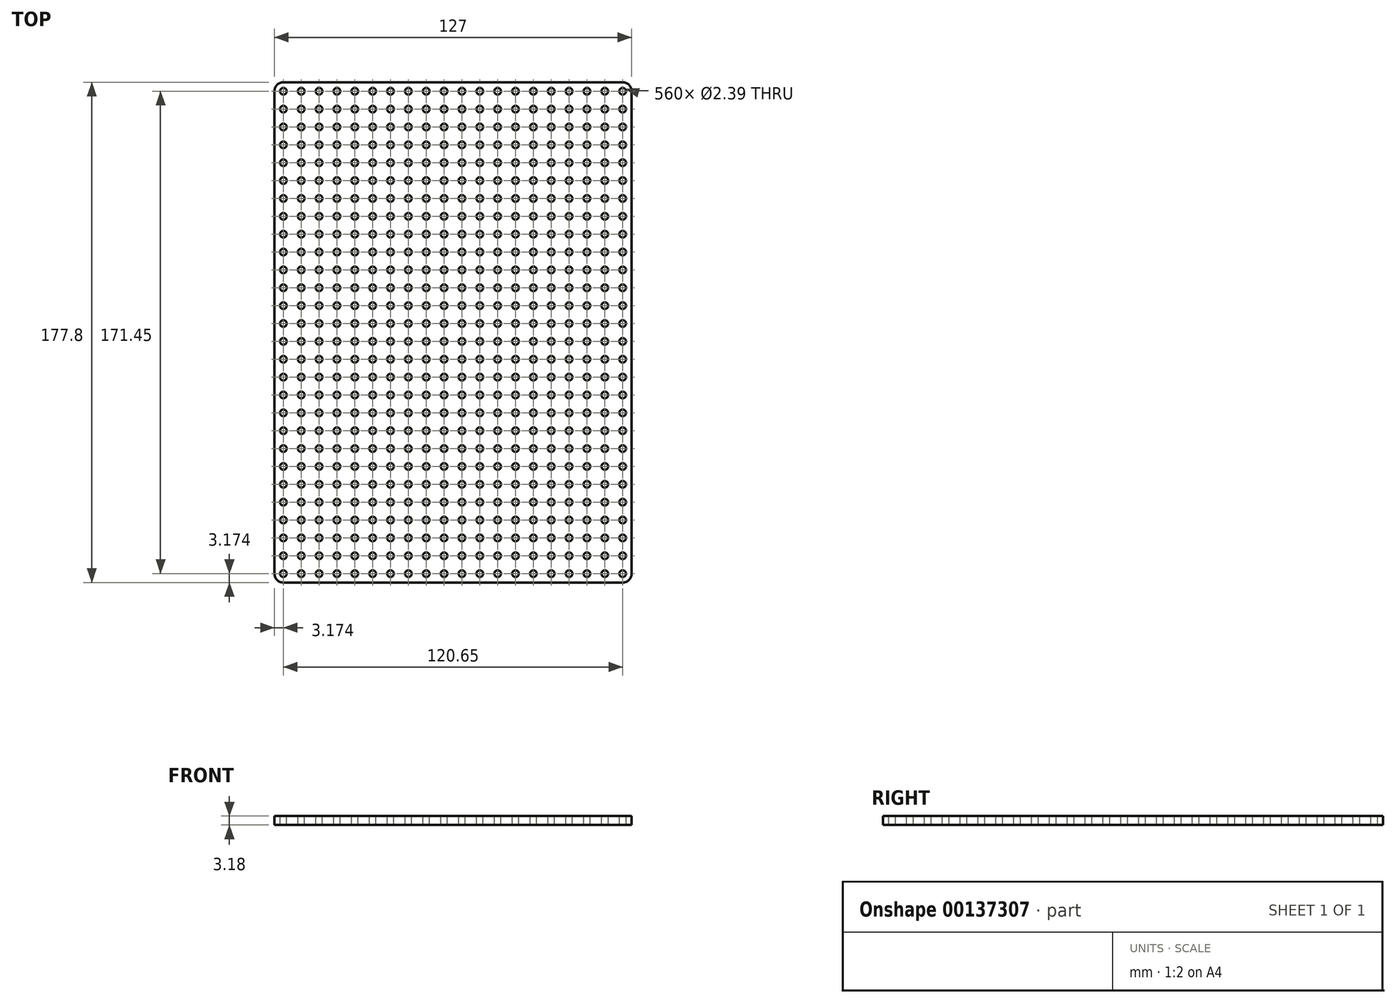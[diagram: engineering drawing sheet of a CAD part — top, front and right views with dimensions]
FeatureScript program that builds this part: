
annotation { "Feature Type Name" : "Feature", "Feature Type Description" : "" }
export const myFeature = defineFeature(function(context is Context, id is Id, definition is map)
    precondition{}
    {
        {
            var Q0;
            Q0=qCreatedBy(makeId("Top.planeOp"),FACE);
            var sketch = newSketch(context, id + "F0", { "sketchPlane" : qUnion([Q0])});
            skLineSegment(sketch, "E0.bottom", {"start": v(-60.72, -89.16) * mm, "end": v(59.93, -89.16) * mm});
            skLineSegment(sketch, "E0.top", {"start": v(-60.72, 88.64) * mm, "end": v(59.93, 88.64) * mm});
            skLineSegment(sketch, "E0.left", {"start": v(-63.9, -85.99) * mm, "end": v(-63.9, 85.46) * mm});
            skLineSegment(sketch, "E0.right", {"start": v(63.1, -85.99) * mm, "end": v(63.1, 85.46) * mm});
            skPoint(sketch, "E1.visualSharp", {"position": v(-63.9, 88.64) * mm});
            skArc(sketch, "E1.filletArc", {"start": v(-60.72, 88.64) * mm, "mid": v(-62.96, 87.7) * mm, "end": v(-63.9, 85.46) * mm});
            skPoint(sketch, "E2.visualSharp", {"position": v(63.1, 88.64) * mm});
            skArc(sketch, "E2.filletArc", {"start": v(63.1, 85.46) * mm, "mid": v(62.18, 87.7) * mm, "end": v(59.93, 88.64) * mm});
            skPoint(sketch, "E3.visualSharp", {"position": v(63.1, -89.16) * mm});
            skArc(sketch, "E3.filletArc", {"start": v(59.93, -89.16) * mm, "mid": v(62.18, -88.23) * mm, "end": v(63.1, -85.99) * mm});
            skPoint(sketch, "E4.visualSharp", {"position": v(-63.9, -89.16) * mm});
            skArc(sketch, "E4.filletArc", {"start": v(-63.9, -85.99) * mm, "mid": v(-62.96, -88.23) * mm, "end": v(-60.72, -89.16) * mm});
            skSolve(sketch);
        }
        {
            var Q0;
            Q0 = qSketchRegion(id + "F0", true);
            extrude(context, id + "F1", {"entities" : qUnion([Q0]), "depth" : 3.17 * mm});
        }
        {
            var Q0;
            Q0=makeQuery(id+"F1.opExtrude","CAP_FACE",FACE,{"disambiguationData":[OSD([sQuery(id+"F0.wireOp",EDGE,"E0.bottom"),sQuery(id+"F0.wireOp",EDGE,"E0.top"),sQuery(id+"F0.wireOp",EDGE,"E0.left"),sQuery(id+"F0.wireOp",EDGE,"E0.right"),sQuery(id+"F0.wireOp",EDGE,"E1.filletArc"),sQuery(id+"F0.wireOp",EDGE,"E2.filletArc"),sQuery(id+"F0.wireOp",EDGE,"E3.filletArc"),sQuery(id+"F0.wireOp",EDGE,"E4.filletArc")])],"isStart":false});
            var sketch = newSketch(context, id + "F2", { "sketchPlane" : qUnion([Q0])});
            skCircle(sketch, "E5", {"center": v(-60.72, -85.99) * mm, "radius": 1.2 * mm});
            skCircle(sketch, "E6.0.1.0", {"center": v(-60.72, -79.64) * mm, "radius": 1.2 * mm});
            skCircle(sketch, "E6.0.2.0", {"center": v(-60.72, -73.29) * mm, "radius": 1.2 * mm});
            skCircle(sketch, "E6.0.3.0", {"center": v(-60.72, -66.94) * mm, "radius": 1.2 * mm});
            skCircle(sketch, "E6.0.4.0", {"center": v(-60.72, -60.59) * mm, "radius": 1.2 * mm});
            skCircle(sketch, "E6.0.5.0", {"center": v(-60.72, -54.24) * mm, "radius": 1.2 * mm});
            skCircle(sketch, "E6.0.6.0", {"center": v(-60.72, -47.89) * mm, "radius": 1.2 * mm});
            skCircle(sketch, "E6.0.7.0", {"center": v(-60.72, -41.54) * mm, "radius": 1.2 * mm});
            skCircle(sketch, "E6.0.8.0", {"center": v(-60.72, -35.19) * mm, "radius": 1.2 * mm});
            skCircle(sketch, "E6.0.9.0", {"center": v(-60.72, -28.84) * mm, "radius": 1.2 * mm});
            skCircle(sketch, "E6.0.10.0", {"center": v(-60.72, -22.49) * mm, "radius": 1.2 * mm});
            skCircle(sketch, "E6.0.11.0", {"center": v(-60.72, -16.14) * mm, "radius": 1.2 * mm});
            skCircle(sketch, "E6.0.12.0", {"center": v(-60.72, -9.79) * mm, "radius": 1.2 * mm});
            skCircle(sketch, "E6.0.13.0", {"center": v(-60.72, -3.44) * mm, "radius": 1.2 * mm});
            skCircle(sketch, "E6.0.14.0", {"center": v(-60.72, 2.91) * mm, "radius": 1.2 * mm});
            skCircle(sketch, "E6.0.15.0", {"center": v(-60.72, 9.26) * mm, "radius": 1.2 * mm});
            skCircle(sketch, "E6.0.16.0", {"center": v(-60.72, 15.61) * mm, "radius": 1.2 * mm});
            skCircle(sketch, "E6.0.17.0", {"center": v(-60.72, 21.96) * mm, "radius": 1.2 * mm});
            skCircle(sketch, "E6.0.18.0", {"center": v(-60.72, 28.31) * mm, "radius": 1.2 * mm});
            skCircle(sketch, "E6.0.19.0", {"center": v(-60.72, 34.66) * mm, "radius": 1.2 * mm});
            skCircle(sketch, "E6.0.20.0", {"center": v(-60.72, 41.01) * mm, "radius": 1.2 * mm});
            skCircle(sketch, "E6.0.21.0", {"center": v(-60.72, 47.36) * mm, "radius": 1.2 * mm});
            skCircle(sketch, "E6.0.22.0", {"center": v(-60.72, 53.71) * mm, "radius": 1.2 * mm});
            skCircle(sketch, "E6.0.23.0", {"center": v(-60.72, 60.06) * mm, "radius": 1.2 * mm});
            skCircle(sketch, "E6.0.24.0", {"center": v(-60.72, 66.41) * mm, "radius": 1.2 * mm});
            skCircle(sketch, "E6.0.25.0", {"center": v(-60.72, 72.76) * mm, "radius": 1.2 * mm});
            skCircle(sketch, "E6.0.26.0", {"center": v(-60.72, 79.11) * mm, "radius": 1.2 * mm});
            skCircle(sketch, "E6.0.27.0", {"center": v(-60.72, 85.46) * mm, "radius": 1.2 * mm});
            skCircle(sketch, "E6.1.0.0", {"center": v(-54.37, -85.99) * mm, "radius": 1.2 * mm});
            skCircle(sketch, "E6.1.1.0", {"center": v(-54.37, -79.64) * mm, "radius": 1.2 * mm});
            skCircle(sketch, "E6.1.2.0", {"center": v(-54.37, -73.29) * mm, "radius": 1.2 * mm});
            skCircle(sketch, "E6.1.3.0", {"center": v(-54.37, -66.94) * mm, "radius": 1.2 * mm});
            skCircle(sketch, "E6.1.4.0", {"center": v(-54.37, -60.59) * mm, "radius": 1.2 * mm});
            skCircle(sketch, "E6.1.5.0", {"center": v(-54.37, -54.24) * mm, "radius": 1.2 * mm});
            skCircle(sketch, "E6.1.6.0", {"center": v(-54.37, -47.89) * mm, "radius": 1.2 * mm});
            skCircle(sketch, "E6.1.7.0", {"center": v(-54.37, -41.54) * mm, "radius": 1.2 * mm});
            skCircle(sketch, "E6.1.8.0", {"center": v(-54.37, -35.19) * mm, "radius": 1.2 * mm});
            skCircle(sketch, "E6.1.9.0", {"center": v(-54.37, -28.84) * mm, "radius": 1.2 * mm});
            skCircle(sketch, "E6.1.10.0", {"center": v(-54.37, -22.49) * mm, "radius": 1.2 * mm});
            skCircle(sketch, "E6.1.11.0", {"center": v(-54.37, -16.14) * mm, "radius": 1.2 * mm});
            skCircle(sketch, "E6.1.12.0", {"center": v(-54.37, -9.79) * mm, "radius": 1.2 * mm});
            skCircle(sketch, "E6.1.13.0", {"center": v(-54.37, -3.44) * mm, "radius": 1.2 * mm});
            skCircle(sketch, "E6.1.14.0", {"center": v(-54.37, 2.91) * mm, "radius": 1.2 * mm});
            skCircle(sketch, "E6.1.15.0", {"center": v(-54.37, 9.26) * mm, "radius": 1.2 * mm});
            skCircle(sketch, "E6.1.16.0", {"center": v(-54.37, 15.61) * mm, "radius": 1.2 * mm});
            skCircle(sketch, "E6.1.17.0", {"center": v(-54.37, 21.96) * mm, "radius": 1.2 * mm});
            skCircle(sketch, "E6.1.18.0", {"center": v(-54.37, 28.31) * mm, "radius": 1.2 * mm});
            skCircle(sketch, "E6.1.19.0", {"center": v(-54.37, 34.66) * mm, "radius": 1.2 * mm});
            skCircle(sketch, "E6.1.20.0", {"center": v(-54.37, 41.01) * mm, "radius": 1.2 * mm});
            skCircle(sketch, "E6.1.21.0", {"center": v(-54.37, 47.36) * mm, "radius": 1.2 * mm});
            skCircle(sketch, "E6.1.22.0", {"center": v(-54.37, 53.71) * mm, "radius": 1.2 * mm});
            skCircle(sketch, "E6.1.23.0", {"center": v(-54.37, 60.06) * mm, "radius": 1.2 * mm});
            skCircle(sketch, "E6.1.24.0", {"center": v(-54.37, 66.41) * mm, "radius": 1.2 * mm});
            skCircle(sketch, "E6.1.25.0", {"center": v(-54.37, 72.76) * mm, "radius": 1.2 * mm});
            skCircle(sketch, "E6.1.26.0", {"center": v(-54.37, 79.11) * mm, "radius": 1.2 * mm});
            skCircle(sketch, "E6.1.27.0", {"center": v(-54.37, 85.46) * mm, "radius": 1.2 * mm});
            skCircle(sketch, "E6.2.0.0", {"center": v(-48.02, -85.99) * mm, "radius": 1.2 * mm});
            skCircle(sketch, "E6.2.1.0", {"center": v(-48.02, -79.64) * mm, "radius": 1.2 * mm});
            skCircle(sketch, "E6.2.2.0", {"center": v(-48.02, -73.29) * mm, "radius": 1.2 * mm});
            skCircle(sketch, "E6.2.3.0", {"center": v(-48.02, -66.94) * mm, "radius": 1.2 * mm});
            skCircle(sketch, "E6.2.4.0", {"center": v(-48.02, -60.59) * mm, "radius": 1.2 * mm});
            skCircle(sketch, "E6.2.5.0", {"center": v(-48.02, -54.24) * mm, "radius": 1.2 * mm});
            skCircle(sketch, "E6.2.6.0", {"center": v(-48.02, -47.89) * mm, "radius": 1.2 * mm});
            skCircle(sketch, "E6.2.7.0", {"center": v(-48.02, -41.54) * mm, "radius": 1.2 * mm});
            skCircle(sketch, "E6.2.8.0", {"center": v(-48.02, -35.19) * mm, "radius": 1.2 * mm});
            skCircle(sketch, "E6.2.9.0", {"center": v(-48.02, -28.84) * mm, "radius": 1.2 * mm});
            skCircle(sketch, "E6.2.10.0", {"center": v(-48.02, -22.49) * mm, "radius": 1.2 * mm});
            skCircle(sketch, "E6.2.11.0", {"center": v(-48.02, -16.14) * mm, "radius": 1.2 * mm});
            skCircle(sketch, "E6.2.12.0", {"center": v(-48.02, -9.79) * mm, "radius": 1.2 * mm});
            skCircle(sketch, "E6.2.13.0", {"center": v(-48.02, -3.44) * mm, "radius": 1.2 * mm});
            skCircle(sketch, "E6.2.14.0", {"center": v(-48.02, 2.91) * mm, "radius": 1.2 * mm});
            skCircle(sketch, "E6.2.15.0", {"center": v(-48.02, 9.26) * mm, "radius": 1.2 * mm});
            skCircle(sketch, "E6.2.16.0", {"center": v(-48.02, 15.61) * mm, "radius": 1.2 * mm});
            skCircle(sketch, "E6.2.17.0", {"center": v(-48.02, 21.96) * mm, "radius": 1.2 * mm});
            skCircle(sketch, "E6.2.18.0", {"center": v(-48.02, 28.31) * mm, "radius": 1.2 * mm});
            skCircle(sketch, "E6.2.19.0", {"center": v(-48.02, 34.66) * mm, "radius": 1.2 * mm});
            skCircle(sketch, "E6.2.20.0", {"center": v(-48.02, 41.01) * mm, "radius": 1.2 * mm});
            skCircle(sketch, "E6.2.21.0", {"center": v(-48.02, 47.36) * mm, "radius": 1.2 * mm});
            skCircle(sketch, "E6.2.22.0", {"center": v(-48.02, 53.71) * mm, "radius": 1.2 * mm});
            skCircle(sketch, "E6.2.23.0", {"center": v(-48.02, 60.06) * mm, "radius": 1.2 * mm});
            skCircle(sketch, "E6.2.24.0", {"center": v(-48.02, 66.41) * mm, "radius": 1.2 * mm});
            skCircle(sketch, "E6.2.25.0", {"center": v(-48.02, 72.76) * mm, "radius": 1.2 * mm});
            skCircle(sketch, "E6.2.26.0", {"center": v(-48.02, 79.11) * mm, "radius": 1.2 * mm});
            skCircle(sketch, "E6.2.27.0", {"center": v(-48.02, 85.46) * mm, "radius": 1.2 * mm});
            skCircle(sketch, "E6.3.0.0", {"center": v(-41.67, -85.99) * mm, "radius": 1.2 * mm});
            skCircle(sketch, "E6.3.1.0", {"center": v(-41.67, -79.64) * mm, "radius": 1.2 * mm});
            skCircle(sketch, "E6.3.2.0", {"center": v(-41.67, -73.29) * mm, "radius": 1.2 * mm});
            skCircle(sketch, "E6.3.3.0", {"center": v(-41.67, -66.94) * mm, "radius": 1.2 * mm});
            skCircle(sketch, "E6.3.4.0", {"center": v(-41.67, -60.59) * mm, "radius": 1.2 * mm});
            skCircle(sketch, "E6.3.5.0", {"center": v(-41.67, -54.24) * mm, "radius": 1.2 * mm});
            skCircle(sketch, "E6.3.6.0", {"center": v(-41.67, -47.89) * mm, "radius": 1.2 * mm});
            skCircle(sketch, "E6.3.7.0", {"center": v(-41.67, -41.54) * mm, "radius": 1.2 * mm});
            skCircle(sketch, "E6.3.8.0", {"center": v(-41.67, -35.19) * mm, "radius": 1.2 * mm});
            skCircle(sketch, "E6.3.9.0", {"center": v(-41.67, -28.84) * mm, "radius": 1.2 * mm});
            skCircle(sketch, "E6.3.10.0", {"center": v(-41.67, -22.49) * mm, "radius": 1.2 * mm});
            skCircle(sketch, "E6.3.11.0", {"center": v(-41.67, -16.14) * mm, "radius": 1.2 * mm});
            skCircle(sketch, "E6.3.12.0", {"center": v(-41.67, -9.79) * mm, "radius": 1.2 * mm});
            skCircle(sketch, "E6.3.13.0", {"center": v(-41.67, -3.44) * mm, "radius": 1.2 * mm});
            skCircle(sketch, "E6.3.14.0", {"center": v(-41.67, 2.91) * mm, "radius": 1.2 * mm});
            skCircle(sketch, "E6.3.15.0", {"center": v(-41.67, 9.26) * mm, "radius": 1.2 * mm});
            skCircle(sketch, "E6.3.16.0", {"center": v(-41.67, 15.61) * mm, "radius": 1.2 * mm});
            skCircle(sketch, "E6.3.17.0", {"center": v(-41.67, 21.96) * mm, "radius": 1.2 * mm});
            skCircle(sketch, "E6.3.18.0", {"center": v(-41.67, 28.31) * mm, "radius": 1.2 * mm});
            skCircle(sketch, "E6.3.19.0", {"center": v(-41.67, 34.66) * mm, "radius": 1.2 * mm});
            skCircle(sketch, "E6.3.20.0", {"center": v(-41.67, 41.01) * mm, "radius": 1.2 * mm});
            skCircle(sketch, "E6.3.21.0", {"center": v(-41.67, 47.36) * mm, "radius": 1.2 * mm});
            skCircle(sketch, "E6.3.22.0", {"center": v(-41.67, 53.71) * mm, "radius": 1.2 * mm});
            skCircle(sketch, "E6.3.23.0", {"center": v(-41.67, 60.06) * mm, "radius": 1.2 * mm});
            skCircle(sketch, "E6.3.24.0", {"center": v(-41.67, 66.41) * mm, "radius": 1.2 * mm});
            skCircle(sketch, "E6.3.25.0", {"center": v(-41.67, 72.76) * mm, "radius": 1.2 * mm});
            skCircle(sketch, "E6.3.26.0", {"center": v(-41.67, 79.11) * mm, "radius": 1.2 * mm});
            skCircle(sketch, "E6.3.27.0", {"center": v(-41.67, 85.46) * mm, "radius": 1.2 * mm});
            skCircle(sketch, "E6.4.0.0", {"center": v(-35.32, -85.99) * mm, "radius": 1.2 * mm});
            skCircle(sketch, "E6.4.1.0", {"center": v(-35.32, -79.64) * mm, "radius": 1.2 * mm});
            skCircle(sketch, "E6.4.2.0", {"center": v(-35.32, -73.29) * mm, "radius": 1.2 * mm});
            skCircle(sketch, "E6.4.3.0", {"center": v(-35.32, -66.94) * mm, "radius": 1.2 * mm});
            skCircle(sketch, "E6.4.4.0", {"center": v(-35.32, -60.59) * mm, "radius": 1.2 * mm});
            skCircle(sketch, "E6.4.5.0", {"center": v(-35.32, -54.24) * mm, "radius": 1.2 * mm});
            skCircle(sketch, "E6.4.6.0", {"center": v(-35.32, -47.89) * mm, "radius": 1.2 * mm});
            skCircle(sketch, "E6.4.7.0", {"center": v(-35.32, -41.54) * mm, "radius": 1.2 * mm});
            skCircle(sketch, "E6.4.8.0", {"center": v(-35.32, -35.19) * mm, "radius": 1.2 * mm});
            skCircle(sketch, "E6.4.9.0", {"center": v(-35.32, -28.84) * mm, "radius": 1.2 * mm});
            skCircle(sketch, "E6.4.10.0", {"center": v(-35.32, -22.49) * mm, "radius": 1.2 * mm});
            skCircle(sketch, "E6.4.11.0", {"center": v(-35.32, -16.14) * mm, "radius": 1.2 * mm});
            skCircle(sketch, "E6.4.12.0", {"center": v(-35.32, -9.79) * mm, "radius": 1.2 * mm});
            skCircle(sketch, "E6.4.13.0", {"center": v(-35.32, -3.44) * mm, "radius": 1.2 * mm});
            skCircle(sketch, "E6.4.14.0", {"center": v(-35.32, 2.91) * mm, "radius": 1.2 * mm});
            skCircle(sketch, "E6.4.15.0", {"center": v(-35.32, 9.26) * mm, "radius": 1.2 * mm});
            skCircle(sketch, "E6.4.16.0", {"center": v(-35.32, 15.61) * mm, "radius": 1.2 * mm});
            skCircle(sketch, "E6.4.17.0", {"center": v(-35.32, 21.96) * mm, "radius": 1.2 * mm});
            skCircle(sketch, "E6.4.18.0", {"center": v(-35.32, 28.31) * mm, "radius": 1.2 * mm});
            skCircle(sketch, "E6.4.19.0", {"center": v(-35.32, 34.66) * mm, "radius": 1.2 * mm});
            skCircle(sketch, "E6.4.20.0", {"center": v(-35.32, 41.01) * mm, "radius": 1.2 * mm});
            skCircle(sketch, "E6.4.21.0", {"center": v(-35.32, 47.36) * mm, "radius": 1.2 * mm});
            skCircle(sketch, "E6.4.22.0", {"center": v(-35.32, 53.71) * mm, "radius": 1.2 * mm});
            skCircle(sketch, "E6.4.23.0", {"center": v(-35.32, 60.06) * mm, "radius": 1.2 * mm});
            skCircle(sketch, "E6.4.24.0", {"center": v(-35.32, 66.41) * mm, "radius": 1.2 * mm});
            skCircle(sketch, "E6.4.25.0", {"center": v(-35.32, 72.76) * mm, "radius": 1.2 * mm});
            skCircle(sketch, "E6.4.26.0", {"center": v(-35.32, 79.11) * mm, "radius": 1.2 * mm});
            skCircle(sketch, "E6.4.27.0", {"center": v(-35.32, 85.46) * mm, "radius": 1.2 * mm});
            skCircle(sketch, "E6.5.0.0", {"center": v(-28.97, -85.99) * mm, "radius": 1.2 * mm});
            skCircle(sketch, "E6.5.1.0", {"center": v(-28.97, -79.64) * mm, "radius": 1.2 * mm});
            skCircle(sketch, "E6.5.2.0", {"center": v(-28.97, -73.29) * mm, "radius": 1.2 * mm});
            skCircle(sketch, "E6.5.3.0", {"center": v(-28.97, -66.94) * mm, "radius": 1.2 * mm});
            skCircle(sketch, "E6.5.4.0", {"center": v(-28.97, -60.59) * mm, "radius": 1.2 * mm});
            skCircle(sketch, "E6.5.5.0", {"center": v(-28.97, -54.24) * mm, "radius": 1.2 * mm});
            skCircle(sketch, "E6.5.6.0", {"center": v(-28.97, -47.89) * mm, "radius": 1.2 * mm});
            skCircle(sketch, "E6.5.7.0", {"center": v(-28.97, -41.54) * mm, "radius": 1.2 * mm});
            skCircle(sketch, "E6.5.8.0", {"center": v(-28.97, -35.19) * mm, "radius": 1.2 * mm});
            skCircle(sketch, "E6.5.9.0", {"center": v(-28.97, -28.84) * mm, "radius": 1.2 * mm});
            skCircle(sketch, "E6.5.10.0", {"center": v(-28.97, -22.49) * mm, "radius": 1.2 * mm});
            skCircle(sketch, "E6.5.11.0", {"center": v(-28.97, -16.14) * mm, "radius": 1.2 * mm});
            skCircle(sketch, "E6.5.12.0", {"center": v(-28.97, -9.79) * mm, "radius": 1.2 * mm});
            skCircle(sketch, "E6.5.13.0", {"center": v(-28.97, -3.44) * mm, "radius": 1.2 * mm});
            skCircle(sketch, "E6.5.14.0", {"center": v(-28.97, 2.91) * mm, "radius": 1.2 * mm});
            skCircle(sketch, "E6.5.15.0", {"center": v(-28.97, 9.26) * mm, "radius": 1.2 * mm});
            skCircle(sketch, "E6.5.16.0", {"center": v(-28.97, 15.61) * mm, "radius": 1.2 * mm});
            skCircle(sketch, "E6.5.17.0", {"center": v(-28.97, 21.96) * mm, "radius": 1.2 * mm});
            skCircle(sketch, "E6.5.18.0", {"center": v(-28.97, 28.31) * mm, "radius": 1.2 * mm});
            skCircle(sketch, "E6.5.19.0", {"center": v(-28.97, 34.66) * mm, "radius": 1.2 * mm});
            skCircle(sketch, "E6.5.20.0", {"center": v(-28.97, 41.01) * mm, "radius": 1.2 * mm});
            skCircle(sketch, "E6.5.21.0", {"center": v(-28.97, 47.36) * mm, "radius": 1.2 * mm});
            skCircle(sketch, "E6.5.22.0", {"center": v(-28.97, 53.71) * mm, "radius": 1.2 * mm});
            skCircle(sketch, "E6.5.23.0", {"center": v(-28.97, 60.06) * mm, "radius": 1.2 * mm});
            skCircle(sketch, "E6.5.24.0", {"center": v(-28.97, 66.41) * mm, "radius": 1.2 * mm});
            skCircle(sketch, "E6.5.25.0", {"center": v(-28.97, 72.76) * mm, "radius": 1.2 * mm});
            skCircle(sketch, "E6.5.26.0", {"center": v(-28.97, 79.11) * mm, "radius": 1.2 * mm});
            skCircle(sketch, "E6.5.27.0", {"center": v(-28.97, 85.46) * mm, "radius": 1.2 * mm});
            skCircle(sketch, "E6.6.0.0", {"center": v(-22.62, -85.99) * mm, "radius": 1.2 * mm});
            skCircle(sketch, "E6.6.1.0", {"center": v(-22.62, -79.64) * mm, "radius": 1.2 * mm});
            skCircle(sketch, "E6.6.2.0", {"center": v(-22.62, -73.29) * mm, "radius": 1.2 * mm});
            skCircle(sketch, "E6.6.3.0", {"center": v(-22.62, -66.94) * mm, "radius": 1.2 * mm});
            skCircle(sketch, "E6.6.4.0", {"center": v(-22.62, -60.59) * mm, "radius": 1.2 * mm});
            skCircle(sketch, "E6.6.5.0", {"center": v(-22.62, -54.24) * mm, "radius": 1.2 * mm});
            skCircle(sketch, "E6.6.6.0", {"center": v(-22.62, -47.89) * mm, "radius": 1.2 * mm});
            skCircle(sketch, "E6.6.7.0", {"center": v(-22.62, -41.54) * mm, "radius": 1.2 * mm});
            skCircle(sketch, "E6.6.8.0", {"center": v(-22.62, -35.19) * mm, "radius": 1.2 * mm});
            skCircle(sketch, "E6.6.9.0", {"center": v(-22.62, -28.84) * mm, "radius": 1.2 * mm});
            skCircle(sketch, "E6.6.10.0", {"center": v(-22.62, -22.49) * mm, "radius": 1.2 * mm});
            skCircle(sketch, "E6.6.11.0", {"center": v(-22.62, -16.14) * mm, "radius": 1.2 * mm});
            skCircle(sketch, "E6.6.12.0", {"center": v(-22.62, -9.79) * mm, "radius": 1.2 * mm});
            skCircle(sketch, "E6.6.13.0", {"center": v(-22.62, -3.44) * mm, "radius": 1.2 * mm});
            skCircle(sketch, "E6.6.14.0", {"center": v(-22.62, 2.91) * mm, "radius": 1.2 * mm});
            skCircle(sketch, "E6.6.15.0", {"center": v(-22.62, 9.26) * mm, "radius": 1.2 * mm});
            skCircle(sketch, "E6.6.16.0", {"center": v(-22.62, 15.61) * mm, "radius": 1.2 * mm});
            skCircle(sketch, "E6.6.17.0", {"center": v(-22.62, 21.96) * mm, "radius": 1.2 * mm});
            skCircle(sketch, "E6.6.18.0", {"center": v(-22.62, 28.31) * mm, "radius": 1.2 * mm});
            skCircle(sketch, "E6.6.19.0", {"center": v(-22.62, 34.66) * mm, "radius": 1.2 * mm});
            skCircle(sketch, "E6.6.20.0", {"center": v(-22.62, 41.01) * mm, "radius": 1.2 * mm});
            skCircle(sketch, "E6.6.21.0", {"center": v(-22.62, 47.36) * mm, "radius": 1.2 * mm});
            skCircle(sketch, "E6.6.22.0", {"center": v(-22.62, 53.71) * mm, "radius": 1.2 * mm});
            skCircle(sketch, "E6.6.23.0", {"center": v(-22.62, 60.06) * mm, "radius": 1.2 * mm});
            skCircle(sketch, "E6.6.24.0", {"center": v(-22.62, 66.41) * mm, "radius": 1.2 * mm});
            skCircle(sketch, "E6.6.25.0", {"center": v(-22.62, 72.76) * mm, "radius": 1.2 * mm});
            skCircle(sketch, "E6.6.26.0", {"center": v(-22.62, 79.11) * mm, "radius": 1.2 * mm});
            skCircle(sketch, "E6.6.27.0", {"center": v(-22.62, 85.46) * mm, "radius": 1.2 * mm});
            skCircle(sketch, "E6.7.0.0", {"center": v(-16.27, -85.99) * mm, "radius": 1.2 * mm});
            skCircle(sketch, "E6.7.1.0", {"center": v(-16.27, -79.64) * mm, "radius": 1.2 * mm});
            skCircle(sketch, "E6.7.2.0", {"center": v(-16.27, -73.29) * mm, "radius": 1.2 * mm});
            skCircle(sketch, "E6.7.3.0", {"center": v(-16.27, -66.94) * mm, "radius": 1.2 * mm});
            skCircle(sketch, "E6.7.4.0", {"center": v(-16.27, -60.59) * mm, "radius": 1.2 * mm});
            skCircle(sketch, "E6.7.5.0", {"center": v(-16.27, -54.24) * mm, "radius": 1.2 * mm});
            skCircle(sketch, "E6.7.6.0", {"center": v(-16.27, -47.89) * mm, "radius": 1.2 * mm});
            skCircle(sketch, "E6.7.7.0", {"center": v(-16.27, -41.54) * mm, "radius": 1.2 * mm});
            skCircle(sketch, "E6.7.8.0", {"center": v(-16.27, -35.19) * mm, "radius": 1.2 * mm});
            skCircle(sketch, "E6.7.9.0", {"center": v(-16.27, -28.84) * mm, "radius": 1.2 * mm});
            skCircle(sketch, "E6.7.10.0", {"center": v(-16.27, -22.49) * mm, "radius": 1.2 * mm});
            skCircle(sketch, "E6.7.11.0", {"center": v(-16.27, -16.14) * mm, "radius": 1.2 * mm});
            skCircle(sketch, "E6.7.12.0", {"center": v(-16.27, -9.79) * mm, "radius": 1.2 * mm});
            skCircle(sketch, "E6.7.13.0", {"center": v(-16.27, -3.44) * mm, "radius": 1.2 * mm});
            skCircle(sketch, "E6.7.14.0", {"center": v(-16.27, 2.91) * mm, "radius": 1.2 * mm});
            skCircle(sketch, "E6.7.15.0", {"center": v(-16.27, 9.26) * mm, "radius": 1.2 * mm});
            skCircle(sketch, "E6.7.16.0", {"center": v(-16.27, 15.61) * mm, "radius": 1.2 * mm});
            skCircle(sketch, "E6.7.17.0", {"center": v(-16.27, 21.96) * mm, "radius": 1.2 * mm});
            skCircle(sketch, "E6.7.18.0", {"center": v(-16.27, 28.31) * mm, "radius": 1.2 * mm});
            skCircle(sketch, "E6.7.19.0", {"center": v(-16.27, 34.66) * mm, "radius": 1.2 * mm});
            skCircle(sketch, "E6.7.20.0", {"center": v(-16.27, 41.01) * mm, "radius": 1.2 * mm});
            skCircle(sketch, "E6.7.21.0", {"center": v(-16.27, 47.36) * mm, "radius": 1.2 * mm});
            skCircle(sketch, "E6.7.22.0", {"center": v(-16.27, 53.71) * mm, "radius": 1.2 * mm});
            skCircle(sketch, "E6.7.23.0", {"center": v(-16.27, 60.06) * mm, "radius": 1.2 * mm});
            skCircle(sketch, "E6.7.24.0", {"center": v(-16.27, 66.41) * mm, "radius": 1.2 * mm});
            skCircle(sketch, "E6.7.25.0", {"center": v(-16.27, 72.76) * mm, "radius": 1.2 * mm});
            skCircle(sketch, "E6.7.26.0", {"center": v(-16.27, 79.11) * mm, "radius": 1.2 * mm});
            skCircle(sketch, "E6.7.27.0", {"center": v(-16.27, 85.46) * mm, "radius": 1.2 * mm});
            skCircle(sketch, "E6.8.0.0", {"center": v(-9.92, -85.99) * mm, "radius": 1.2 * mm});
            skCircle(sketch, "E6.8.1.0", {"center": v(-9.92, -79.64) * mm, "radius": 1.2 * mm});
            skCircle(sketch, "E6.8.2.0", {"center": v(-9.92, -73.29) * mm, "radius": 1.2 * mm});
            skCircle(sketch, "E6.8.3.0", {"center": v(-9.92, -66.94) * mm, "radius": 1.2 * mm});
            skCircle(sketch, "E6.8.4.0", {"center": v(-9.92, -60.59) * mm, "radius": 1.2 * mm});
            skCircle(sketch, "E6.8.5.0", {"center": v(-9.92, -54.24) * mm, "radius": 1.2 * mm});
            skCircle(sketch, "E6.8.6.0", {"center": v(-9.92, -47.89) * mm, "radius": 1.2 * mm});
            skCircle(sketch, "E6.8.7.0", {"center": v(-9.92, -41.54) * mm, "radius": 1.2 * mm});
            skCircle(sketch, "E6.8.8.0", {"center": v(-9.92, -35.19) * mm, "radius": 1.2 * mm});
            skCircle(sketch, "E6.8.9.0", {"center": v(-9.92, -28.84) * mm, "radius": 1.2 * mm});
            skCircle(sketch, "E6.8.10.0", {"center": v(-9.92, -22.49) * mm, "radius": 1.2 * mm});
            skCircle(sketch, "E6.8.11.0", {"center": v(-9.92, -16.14) * mm, "radius": 1.2 * mm});
            skCircle(sketch, "E6.8.12.0", {"center": v(-9.92, -9.79) * mm, "radius": 1.2 * mm});
            skCircle(sketch, "E6.8.13.0", {"center": v(-9.92, -3.44) * mm, "radius": 1.2 * mm});
            skCircle(sketch, "E6.8.14.0", {"center": v(-9.92, 2.91) * mm, "radius": 1.2 * mm});
            skCircle(sketch, "E6.8.15.0", {"center": v(-9.92, 9.26) * mm, "radius": 1.2 * mm});
            skCircle(sketch, "E6.8.16.0", {"center": v(-9.92, 15.61) * mm, "radius": 1.2 * mm});
            skCircle(sketch, "E6.8.17.0", {"center": v(-9.92, 21.96) * mm, "radius": 1.2 * mm});
            skCircle(sketch, "E6.8.18.0", {"center": v(-9.92, 28.31) * mm, "radius": 1.2 * mm});
            skCircle(sketch, "E6.8.19.0", {"center": v(-9.92, 34.66) * mm, "radius": 1.2 * mm});
            skCircle(sketch, "E6.8.20.0", {"center": v(-9.92, 41.01) * mm, "radius": 1.2 * mm});
            skCircle(sketch, "E6.8.21.0", {"center": v(-9.92, 47.36) * mm, "radius": 1.2 * mm});
            skCircle(sketch, "E6.8.22.0", {"center": v(-9.92, 53.71) * mm, "radius": 1.2 * mm});
            skCircle(sketch, "E6.8.23.0", {"center": v(-9.92, 60.06) * mm, "radius": 1.2 * mm});
            skCircle(sketch, "E6.8.24.0", {"center": v(-9.92, 66.41) * mm, "radius": 1.2 * mm});
            skCircle(sketch, "E6.8.25.0", {"center": v(-9.92, 72.76) * mm, "radius": 1.2 * mm});
            skCircle(sketch, "E6.8.26.0", {"center": v(-9.92, 79.11) * mm, "radius": 1.2 * mm});
            skCircle(sketch, "E6.8.27.0", {"center": v(-9.92, 85.46) * mm, "radius": 1.2 * mm});
            skCircle(sketch, "E6.9.0.0", {"center": v(-3.57, -85.99) * mm, "radius": 1.2 * mm});
            skCircle(sketch, "E6.9.1.0", {"center": v(-3.57, -79.64) * mm, "radius": 1.2 * mm});
            skCircle(sketch, "E6.9.2.0", {"center": v(-3.57, -73.29) * mm, "radius": 1.2 * mm});
            skCircle(sketch, "E6.9.3.0", {"center": v(-3.57, -66.94) * mm, "radius": 1.2 * mm});
            skCircle(sketch, "E6.9.4.0", {"center": v(-3.57, -60.59) * mm, "radius": 1.2 * mm});
            skCircle(sketch, "E6.9.5.0", {"center": v(-3.57, -54.24) * mm, "radius": 1.2 * mm});
            skCircle(sketch, "E6.9.6.0", {"center": v(-3.57, -47.89) * mm, "radius": 1.2 * mm});
            skCircle(sketch, "E6.9.7.0", {"center": v(-3.57, -41.54) * mm, "radius": 1.2 * mm});
            skCircle(sketch, "E6.9.8.0", {"center": v(-3.57, -35.19) * mm, "radius": 1.2 * mm});
            skCircle(sketch, "E6.9.9.0", {"center": v(-3.57, -28.84) * mm, "radius": 1.2 * mm});
            skCircle(sketch, "E6.9.10.0", {"center": v(-3.57, -22.49) * mm, "radius": 1.2 * mm});
            skCircle(sketch, "E6.9.11.0", {"center": v(-3.57, -16.14) * mm, "radius": 1.2 * mm});
            skCircle(sketch, "E6.9.12.0", {"center": v(-3.57, -9.79) * mm, "radius": 1.2 * mm});
            skCircle(sketch, "E6.9.13.0", {"center": v(-3.57, -3.44) * mm, "radius": 1.2 * mm});
            skCircle(sketch, "E6.9.14.0", {"center": v(-3.57, 2.91) * mm, "radius": 1.2 * mm});
            skCircle(sketch, "E6.9.15.0", {"center": v(-3.57, 9.26) * mm, "radius": 1.2 * mm});
            skCircle(sketch, "E6.9.16.0", {"center": v(-3.57, 15.61) * mm, "radius": 1.2 * mm});
            skCircle(sketch, "E6.9.17.0", {"center": v(-3.57, 21.96) * mm, "radius": 1.2 * mm});
            skCircle(sketch, "E6.9.18.0", {"center": v(-3.57, 28.31) * mm, "radius": 1.2 * mm});
            skCircle(sketch, "E6.9.19.0", {"center": v(-3.57, 34.66) * mm, "radius": 1.2 * mm});
            skCircle(sketch, "E6.9.20.0", {"center": v(-3.57, 41.01) * mm, "radius": 1.2 * mm});
            skCircle(sketch, "E6.9.21.0", {"center": v(-3.57, 47.36) * mm, "radius": 1.2 * mm});
            skCircle(sketch, "E6.9.22.0", {"center": v(-3.57, 53.71) * mm, "radius": 1.2 * mm});
            skCircle(sketch, "E6.9.23.0", {"center": v(-3.57, 60.06) * mm, "radius": 1.2 * mm});
            skCircle(sketch, "E6.9.24.0", {"center": v(-3.57, 66.41) * mm, "radius": 1.2 * mm});
            skCircle(sketch, "E6.9.25.0", {"center": v(-3.57, 72.76) * mm, "radius": 1.2 * mm});
            skCircle(sketch, "E6.9.26.0", {"center": v(-3.57, 79.11) * mm, "radius": 1.2 * mm});
            skCircle(sketch, "E6.9.27.0", {"center": v(-3.57, 85.46) * mm, "radius": 1.2 * mm});
            skCircle(sketch, "E6.10.0.0", {"center": v(2.78, -85.99) * mm, "radius": 1.2 * mm});
            skCircle(sketch, "E6.10.1.0", {"center": v(2.78, -79.64) * mm, "radius": 1.2 * mm});
            skCircle(sketch, "E6.10.2.0", {"center": v(2.78, -73.29) * mm, "radius": 1.2 * mm});
            skCircle(sketch, "E6.10.3.0", {"center": v(2.78, -66.94) * mm, "radius": 1.2 * mm});
            skCircle(sketch, "E6.10.4.0", {"center": v(2.78, -60.59) * mm, "radius": 1.2 * mm});
            skCircle(sketch, "E6.10.5.0", {"center": v(2.78, -54.24) * mm, "radius": 1.2 * mm});
            skCircle(sketch, "E6.10.6.0", {"center": v(2.78, -47.89) * mm, "radius": 1.2 * mm});
            skCircle(sketch, "E6.10.7.0", {"center": v(2.78, -41.54) * mm, "radius": 1.2 * mm});
            skCircle(sketch, "E6.10.8.0", {"center": v(2.78, -35.19) * mm, "radius": 1.2 * mm});
            skCircle(sketch, "E6.10.9.0", {"center": v(2.78, -28.84) * mm, "radius": 1.2 * mm});
            skCircle(sketch, "E6.10.10.0", {"center": v(2.78, -22.49) * mm, "radius": 1.2 * mm});
            skCircle(sketch, "E6.10.11.0", {"center": v(2.78, -16.14) * mm, "radius": 1.2 * mm});
            skCircle(sketch, "E6.10.12.0", {"center": v(2.78, -9.79) * mm, "radius": 1.2 * mm});
            skCircle(sketch, "E6.10.13.0", {"center": v(2.78, -3.44) * mm, "radius": 1.2 * mm});
            skCircle(sketch, "E6.10.14.0", {"center": v(2.78, 2.91) * mm, "radius": 1.2 * mm});
            skCircle(sketch, "E6.10.15.0", {"center": v(2.78, 9.26) * mm, "radius": 1.2 * mm});
            skCircle(sketch, "E6.10.16.0", {"center": v(2.78, 15.61) * mm, "radius": 1.2 * mm});
            skCircle(sketch, "E6.10.17.0", {"center": v(2.78, 21.96) * mm, "radius": 1.2 * mm});
            skCircle(sketch, "E6.10.18.0", {"center": v(2.78, 28.31) * mm, "radius": 1.2 * mm});
            skCircle(sketch, "E6.10.19.0", {"center": v(2.78, 34.66) * mm, "radius": 1.2 * mm});
            skCircle(sketch, "E6.10.20.0", {"center": v(2.78, 41.01) * mm, "radius": 1.2 * mm});
            skCircle(sketch, "E6.10.21.0", {"center": v(2.78, 47.36) * mm, "radius": 1.2 * mm});
            skCircle(sketch, "E6.10.22.0", {"center": v(2.78, 53.71) * mm, "radius": 1.2 * mm});
            skCircle(sketch, "E6.10.23.0", {"center": v(2.78, 60.06) * mm, "radius": 1.2 * mm});
            skCircle(sketch, "E6.10.24.0", {"center": v(2.78, 66.41) * mm, "radius": 1.2 * mm});
            skCircle(sketch, "E6.10.25.0", {"center": v(2.78, 72.76) * mm, "radius": 1.2 * mm});
            skCircle(sketch, "E6.10.26.0", {"center": v(2.78, 79.11) * mm, "radius": 1.2 * mm});
            skCircle(sketch, "E6.10.27.0", {"center": v(2.78, 85.46) * mm, "radius": 1.2 * mm});
            skCircle(sketch, "E6.11.0.0", {"center": v(9.13, -85.99) * mm, "radius": 1.2 * mm});
            skCircle(sketch, "E6.11.1.0", {"center": v(9.13, -79.64) * mm, "radius": 1.2 * mm});
            skCircle(sketch, "E6.11.2.0", {"center": v(9.13, -73.29) * mm, "radius": 1.2 * mm});
            skCircle(sketch, "E6.11.3.0", {"center": v(9.13, -66.94) * mm, "radius": 1.2 * mm});
            skCircle(sketch, "E6.11.4.0", {"center": v(9.13, -60.59) * mm, "radius": 1.2 * mm});
            skCircle(sketch, "E6.11.5.0", {"center": v(9.13, -54.24) * mm, "radius": 1.2 * mm});
            skCircle(sketch, "E6.11.6.0", {"center": v(9.13, -47.89) * mm, "radius": 1.2 * mm});
            skCircle(sketch, "E6.11.7.0", {"center": v(9.13, -41.54) * mm, "radius": 1.2 * mm});
            skCircle(sketch, "E6.11.8.0", {"center": v(9.13, -35.19) * mm, "radius": 1.2 * mm});
            skCircle(sketch, "E6.11.9.0", {"center": v(9.13, -28.84) * mm, "radius": 1.2 * mm});
            skCircle(sketch, "E6.11.10.0", {"center": v(9.13, -22.49) * mm, "radius": 1.2 * mm});
            skCircle(sketch, "E6.11.11.0", {"center": v(9.13, -16.14) * mm, "radius": 1.2 * mm});
            skCircle(sketch, "E6.11.12.0", {"center": v(9.13, -9.79) * mm, "radius": 1.2 * mm});
            skCircle(sketch, "E6.11.13.0", {"center": v(9.13, -3.44) * mm, "radius": 1.2 * mm});
            skCircle(sketch, "E6.11.14.0", {"center": v(9.13, 2.91) * mm, "radius": 1.2 * mm});
            skCircle(sketch, "E6.11.15.0", {"center": v(9.13, 9.26) * mm, "radius": 1.2 * mm});
            skCircle(sketch, "E6.11.16.0", {"center": v(9.13, 15.61) * mm, "radius": 1.2 * mm});
            skCircle(sketch, "E6.11.17.0", {"center": v(9.13, 21.96) * mm, "radius": 1.2 * mm});
            skCircle(sketch, "E6.11.18.0", {"center": v(9.13, 28.31) * mm, "radius": 1.2 * mm});
            skCircle(sketch, "E6.11.19.0", {"center": v(9.13, 34.66) * mm, "radius": 1.2 * mm});
            skCircle(sketch, "E6.11.20.0", {"center": v(9.13, 41.01) * mm, "radius": 1.2 * mm});
            skCircle(sketch, "E6.11.21.0", {"center": v(9.13, 47.36) * mm, "radius": 1.2 * mm});
            skCircle(sketch, "E6.11.22.0", {"center": v(9.13, 53.71) * mm, "radius": 1.2 * mm});
            skCircle(sketch, "E6.11.23.0", {"center": v(9.13, 60.06) * mm, "radius": 1.2 * mm});
            skCircle(sketch, "E6.11.24.0", {"center": v(9.13, 66.41) * mm, "radius": 1.2 * mm});
            skCircle(sketch, "E6.11.25.0", {"center": v(9.13, 72.76) * mm, "radius": 1.2 * mm});
            skCircle(sketch, "E6.11.26.0", {"center": v(9.13, 79.11) * mm, "radius": 1.2 * mm});
            skCircle(sketch, "E6.11.27.0", {"center": v(9.13, 85.46) * mm, "radius": 1.2 * mm});
            skCircle(sketch, "E6.12.0.0", {"center": v(15.48, -85.99) * mm, "radius": 1.2 * mm});
            skCircle(sketch, "E6.12.1.0", {"center": v(15.48, -79.64) * mm, "radius": 1.2 * mm});
            skCircle(sketch, "E6.12.2.0", {"center": v(15.48, -73.29) * mm, "radius": 1.2 * mm});
            skCircle(sketch, "E6.12.3.0", {"center": v(15.48, -66.94) * mm, "radius": 1.2 * mm});
            skCircle(sketch, "E6.12.4.0", {"center": v(15.48, -60.59) * mm, "radius": 1.2 * mm});
            skCircle(sketch, "E6.12.5.0", {"center": v(15.48, -54.24) * mm, "radius": 1.2 * mm});
            skCircle(sketch, "E6.12.6.0", {"center": v(15.48, -47.89) * mm, "radius": 1.2 * mm});
            skCircle(sketch, "E6.12.7.0", {"center": v(15.48, -41.54) * mm, "radius": 1.2 * mm});
            skCircle(sketch, "E6.12.8.0", {"center": v(15.48, -35.19) * mm, "radius": 1.2 * mm});
            skCircle(sketch, "E6.12.9.0", {"center": v(15.48, -28.84) * mm, "radius": 1.2 * mm});
            skCircle(sketch, "E6.12.10.0", {"center": v(15.48, -22.49) * mm, "radius": 1.2 * mm});
            skCircle(sketch, "E6.12.11.0", {"center": v(15.48, -16.14) * mm, "radius": 1.2 * mm});
            skCircle(sketch, "E6.12.12.0", {"center": v(15.48, -9.79) * mm, "radius": 1.2 * mm});
            skCircle(sketch, "E6.12.13.0", {"center": v(15.48, -3.44) * mm, "radius": 1.2 * mm});
            skCircle(sketch, "E6.12.14.0", {"center": v(15.48, 2.91) * mm, "radius": 1.2 * mm});
            skCircle(sketch, "E6.12.15.0", {"center": v(15.48, 9.26) * mm, "radius": 1.2 * mm});
            skCircle(sketch, "E6.12.16.0", {"center": v(15.48, 15.61) * mm, "radius": 1.2 * mm});
            skCircle(sketch, "E6.12.17.0", {"center": v(15.48, 21.96) * mm, "radius": 1.2 * mm});
            skCircle(sketch, "E6.12.18.0", {"center": v(15.48, 28.31) * mm, "radius": 1.2 * mm});
            skCircle(sketch, "E6.12.19.0", {"center": v(15.48, 34.66) * mm, "radius": 1.2 * mm});
            skCircle(sketch, "E6.12.20.0", {"center": v(15.48, 41.01) * mm, "radius": 1.2 * mm});
            skCircle(sketch, "E6.12.21.0", {"center": v(15.48, 47.36) * mm, "radius": 1.2 * mm});
            skCircle(sketch, "E6.12.22.0", {"center": v(15.48, 53.71) * mm, "radius": 1.2 * mm});
            skCircle(sketch, "E6.12.23.0", {"center": v(15.48, 60.06) * mm, "radius": 1.2 * mm});
            skCircle(sketch, "E6.12.24.0", {"center": v(15.48, 66.41) * mm, "radius": 1.2 * mm});
            skCircle(sketch, "E6.12.25.0", {"center": v(15.48, 72.76) * mm, "radius": 1.2 * mm});
            skCircle(sketch, "E6.12.26.0", {"center": v(15.48, 79.11) * mm, "radius": 1.2 * mm});
            skCircle(sketch, "E6.12.27.0", {"center": v(15.48, 85.46) * mm, "radius": 1.2 * mm});
            skCircle(sketch, "E6.13.0.0", {"center": v(21.83, -85.99) * mm, "radius": 1.2 * mm});
            skCircle(sketch, "E6.13.1.0", {"center": v(21.83, -79.64) * mm, "radius": 1.2 * mm});
            skCircle(sketch, "E6.13.2.0", {"center": v(21.83, -73.29) * mm, "radius": 1.2 * mm});
            skCircle(sketch, "E6.13.3.0", {"center": v(21.83, -66.94) * mm, "radius": 1.2 * mm});
            skCircle(sketch, "E6.13.4.0", {"center": v(21.83, -60.59) * mm, "radius": 1.2 * mm});
            skCircle(sketch, "E6.13.5.0", {"center": v(21.83, -54.24) * mm, "radius": 1.2 * mm});
            skCircle(sketch, "E6.13.6.0", {"center": v(21.83, -47.89) * mm, "radius": 1.2 * mm});
            skCircle(sketch, "E6.13.7.0", {"center": v(21.83, -41.54) * mm, "radius": 1.2 * mm});
            skCircle(sketch, "E6.13.8.0", {"center": v(21.83, -35.19) * mm, "radius": 1.2 * mm});
            skCircle(sketch, "E6.13.9.0", {"center": v(21.83, -28.84) * mm, "radius": 1.2 * mm});
            skCircle(sketch, "E6.13.10.0", {"center": v(21.83, -22.49) * mm, "radius": 1.2 * mm});
            skCircle(sketch, "E6.13.11.0", {"center": v(21.83, -16.14) * mm, "radius": 1.2 * mm});
            skCircle(sketch, "E6.13.12.0", {"center": v(21.83, -9.79) * mm, "radius": 1.2 * mm});
            skCircle(sketch, "E6.13.13.0", {"center": v(21.83, -3.44) * mm, "radius": 1.2 * mm});
            skCircle(sketch, "E6.13.14.0", {"center": v(21.83, 2.91) * mm, "radius": 1.2 * mm});
            skCircle(sketch, "E6.13.15.0", {"center": v(21.83, 9.26) * mm, "radius": 1.2 * mm});
            skCircle(sketch, "E6.13.16.0", {"center": v(21.83, 15.61) * mm, "radius": 1.2 * mm});
            skCircle(sketch, "E6.13.17.0", {"center": v(21.83, 21.96) * mm, "radius": 1.2 * mm});
            skCircle(sketch, "E6.13.18.0", {"center": v(21.83, 28.31) * mm, "radius": 1.2 * mm});
            skCircle(sketch, "E6.13.19.0", {"center": v(21.83, 34.66) * mm, "radius": 1.2 * mm});
            skCircle(sketch, "E6.13.20.0", {"center": v(21.83, 41.01) * mm, "radius": 1.2 * mm});
            skCircle(sketch, "E6.13.21.0", {"center": v(21.83, 47.36) * mm, "radius": 1.2 * mm});
            skCircle(sketch, "E6.13.22.0", {"center": v(21.83, 53.71) * mm, "radius": 1.2 * mm});
            skCircle(sketch, "E6.13.23.0", {"center": v(21.83, 60.06) * mm, "radius": 1.2 * mm});
            skCircle(sketch, "E6.13.24.0", {"center": v(21.83, 66.41) * mm, "radius": 1.2 * mm});
            skCircle(sketch, "E6.13.25.0", {"center": v(21.83, 72.76) * mm, "radius": 1.2 * mm});
            skCircle(sketch, "E6.13.26.0", {"center": v(21.83, 79.11) * mm, "radius": 1.2 * mm});
            skCircle(sketch, "E6.13.27.0", {"center": v(21.83, 85.46) * mm, "radius": 1.2 * mm});
            skCircle(sketch, "E6.14.0.0", {"center": v(28.18, -85.99) * mm, "radius": 1.2 * mm});
            skCircle(sketch, "E6.14.1.0", {"center": v(28.18, -79.64) * mm, "radius": 1.2 * mm});
            skCircle(sketch, "E6.14.2.0", {"center": v(28.18, -73.29) * mm, "radius": 1.2 * mm});
            skCircle(sketch, "E6.14.3.0", {"center": v(28.18, -66.94) * mm, "radius": 1.2 * mm});
            skCircle(sketch, "E6.14.4.0", {"center": v(28.18, -60.59) * mm, "radius": 1.2 * mm});
            skCircle(sketch, "E6.14.5.0", {"center": v(28.18, -54.24) * mm, "radius": 1.2 * mm});
            skCircle(sketch, "E6.14.6.0", {"center": v(28.18, -47.89) * mm, "radius": 1.2 * mm});
            skCircle(sketch, "E6.14.7.0", {"center": v(28.18, -41.54) * mm, "radius": 1.2 * mm});
            skCircle(sketch, "E6.14.8.0", {"center": v(28.18, -35.19) * mm, "radius": 1.2 * mm});
            skCircle(sketch, "E6.14.9.0", {"center": v(28.18, -28.84) * mm, "radius": 1.2 * mm});
            skCircle(sketch, "E6.14.10.0", {"center": v(28.18, -22.49) * mm, "radius": 1.2 * mm});
            skCircle(sketch, "E6.14.11.0", {"center": v(28.18, -16.14) * mm, "radius": 1.2 * mm});
            skCircle(sketch, "E6.14.12.0", {"center": v(28.18, -9.79) * mm, "radius": 1.2 * mm});
            skCircle(sketch, "E6.14.13.0", {"center": v(28.18, -3.44) * mm, "radius": 1.2 * mm});
            skCircle(sketch, "E6.14.14.0", {"center": v(28.18, 2.91) * mm, "radius": 1.2 * mm});
            skCircle(sketch, "E6.14.15.0", {"center": v(28.18, 9.26) * mm, "radius": 1.2 * mm});
            skCircle(sketch, "E6.14.16.0", {"center": v(28.18, 15.61) * mm, "radius": 1.2 * mm});
            skCircle(sketch, "E6.14.17.0", {"center": v(28.18, 21.96) * mm, "radius": 1.2 * mm});
            skCircle(sketch, "E6.14.18.0", {"center": v(28.18, 28.31) * mm, "radius": 1.2 * mm});
            skCircle(sketch, "E6.14.19.0", {"center": v(28.18, 34.66) * mm, "radius": 1.2 * mm});
            skCircle(sketch, "E6.14.20.0", {"center": v(28.18, 41.01) * mm, "radius": 1.2 * mm});
            skCircle(sketch, "E6.14.21.0", {"center": v(28.18, 47.36) * mm, "radius": 1.2 * mm});
            skCircle(sketch, "E6.14.22.0", {"center": v(28.18, 53.71) * mm, "radius": 1.2 * mm});
            skCircle(sketch, "E6.14.23.0", {"center": v(28.18, 60.06) * mm, "radius": 1.2 * mm});
            skCircle(sketch, "E6.14.24.0", {"center": v(28.18, 66.41) * mm, "radius": 1.2 * mm});
            skCircle(sketch, "E6.14.25.0", {"center": v(28.18, 72.76) * mm, "radius": 1.2 * mm});
            skCircle(sketch, "E6.14.26.0", {"center": v(28.18, 79.11) * mm, "radius": 1.2 * mm});
            skCircle(sketch, "E6.14.27.0", {"center": v(28.18, 85.46) * mm, "radius": 1.2 * mm});
            skCircle(sketch, "E6.15.0.0", {"center": v(34.53, -85.99) * mm, "radius": 1.2 * mm});
            skCircle(sketch, "E6.15.1.0", {"center": v(34.53, -79.64) * mm, "radius": 1.2 * mm});
            skCircle(sketch, "E6.15.2.0", {"center": v(34.53, -73.29) * mm, "radius": 1.2 * mm});
            skCircle(sketch, "E6.15.3.0", {"center": v(34.53, -66.94) * mm, "radius": 1.2 * mm});
            skCircle(sketch, "E6.15.4.0", {"center": v(34.53, -60.59) * mm, "radius": 1.2 * mm});
            skCircle(sketch, "E6.15.5.0", {"center": v(34.53, -54.24) * mm, "radius": 1.2 * mm});
            skCircle(sketch, "E6.15.6.0", {"center": v(34.53, -47.89) * mm, "radius": 1.2 * mm});
            skCircle(sketch, "E6.15.7.0", {"center": v(34.53, -41.54) * mm, "radius": 1.2 * mm});
            skCircle(sketch, "E6.15.8.0", {"center": v(34.53, -35.19) * mm, "radius": 1.2 * mm});
            skCircle(sketch, "E6.15.9.0", {"center": v(34.53, -28.84) * mm, "radius": 1.2 * mm});
            skCircle(sketch, "E6.15.10.0", {"center": v(34.53, -22.49) * mm, "radius": 1.2 * mm});
            skCircle(sketch, "E6.15.11.0", {"center": v(34.53, -16.14) * mm, "radius": 1.2 * mm});
            skCircle(sketch, "E6.15.12.0", {"center": v(34.53, -9.79) * mm, "radius": 1.2 * mm});
            skCircle(sketch, "E6.15.13.0", {"center": v(34.53, -3.44) * mm, "radius": 1.2 * mm});
            skCircle(sketch, "E6.15.14.0", {"center": v(34.53, 2.91) * mm, "radius": 1.2 * mm});
            skCircle(sketch, "E6.15.15.0", {"center": v(34.53, 9.26) * mm, "radius": 1.2 * mm});
            skCircle(sketch, "E6.15.16.0", {"center": v(34.53, 15.61) * mm, "radius": 1.2 * mm});
            skCircle(sketch, "E6.15.17.0", {"center": v(34.53, 21.96) * mm, "radius": 1.2 * mm});
            skCircle(sketch, "E6.15.18.0", {"center": v(34.53, 28.31) * mm, "radius": 1.2 * mm});
            skCircle(sketch, "E6.15.19.0", {"center": v(34.53, 34.66) * mm, "radius": 1.2 * mm});
            skCircle(sketch, "E6.15.20.0", {"center": v(34.53, 41.01) * mm, "radius": 1.2 * mm});
            skCircle(sketch, "E6.15.21.0", {"center": v(34.53, 47.36) * mm, "radius": 1.2 * mm});
            skCircle(sketch, "E6.15.22.0", {"center": v(34.53, 53.71) * mm, "radius": 1.2 * mm});
            skCircle(sketch, "E6.15.23.0", {"center": v(34.53, 60.06) * mm, "radius": 1.2 * mm});
            skCircle(sketch, "E6.15.24.0", {"center": v(34.53, 66.41) * mm, "radius": 1.2 * mm});
            skCircle(sketch, "E6.15.25.0", {"center": v(34.53, 72.76) * mm, "radius": 1.2 * mm});
            skCircle(sketch, "E6.15.26.0", {"center": v(34.53, 79.11) * mm, "radius": 1.2 * mm});
            skCircle(sketch, "E6.15.27.0", {"center": v(34.53, 85.46) * mm, "radius": 1.2 * mm});
            skCircle(sketch, "E6.16.0.0", {"center": v(40.88, -85.99) * mm, "radius": 1.2 * mm});
            skCircle(sketch, "E6.16.1.0", {"center": v(40.88, -79.64) * mm, "radius": 1.2 * mm});
            skCircle(sketch, "E6.16.2.0", {"center": v(40.88, -73.29) * mm, "radius": 1.2 * mm});
            skCircle(sketch, "E6.16.3.0", {"center": v(40.88, -66.94) * mm, "radius": 1.2 * mm});
            skCircle(sketch, "E6.16.4.0", {"center": v(40.88, -60.59) * mm, "radius": 1.2 * mm});
            skCircle(sketch, "E6.16.5.0", {"center": v(40.88, -54.24) * mm, "radius": 1.2 * mm});
            skCircle(sketch, "E6.16.6.0", {"center": v(40.88, -47.89) * mm, "radius": 1.2 * mm});
            skCircle(sketch, "E6.16.7.0", {"center": v(40.88, -41.54) * mm, "radius": 1.2 * mm});
            skCircle(sketch, "E6.16.8.0", {"center": v(40.88, -35.19) * mm, "radius": 1.2 * mm});
            skCircle(sketch, "E6.16.9.0", {"center": v(40.88, -28.84) * mm, "radius": 1.2 * mm});
            skCircle(sketch, "E6.16.10.0", {"center": v(40.88, -22.49) * mm, "radius": 1.2 * mm});
            skCircle(sketch, "E6.16.11.0", {"center": v(40.88, -16.14) * mm, "radius": 1.2 * mm});
            skCircle(sketch, "E6.16.12.0", {"center": v(40.88, -9.79) * mm, "radius": 1.2 * mm});
            skCircle(sketch, "E6.16.13.0", {"center": v(40.88, -3.44) * mm, "radius": 1.2 * mm});
            skCircle(sketch, "E6.16.14.0", {"center": v(40.88, 2.91) * mm, "radius": 1.2 * mm});
            skCircle(sketch, "E6.16.15.0", {"center": v(40.88, 9.26) * mm, "radius": 1.2 * mm});
            skCircle(sketch, "E6.16.16.0", {"center": v(40.88, 15.61) * mm, "radius": 1.2 * mm});
            skCircle(sketch, "E6.16.17.0", {"center": v(40.88, 21.96) * mm, "radius": 1.2 * mm});
            skCircle(sketch, "E6.16.18.0", {"center": v(40.88, 28.31) * mm, "radius": 1.2 * mm});
            skCircle(sketch, "E6.16.19.0", {"center": v(40.88, 34.66) * mm, "radius": 1.2 * mm});
            skCircle(sketch, "E6.16.20.0", {"center": v(40.88, 41.01) * mm, "radius": 1.2 * mm});
            skCircle(sketch, "E6.16.21.0", {"center": v(40.88, 47.36) * mm, "radius": 1.2 * mm});
            skCircle(sketch, "E6.16.22.0", {"center": v(40.88, 53.71) * mm, "radius": 1.2 * mm});
            skCircle(sketch, "E6.16.23.0", {"center": v(40.88, 60.06) * mm, "radius": 1.2 * mm});
            skCircle(sketch, "E6.16.24.0", {"center": v(40.88, 66.41) * mm, "radius": 1.2 * mm});
            skCircle(sketch, "E6.16.25.0", {"center": v(40.88, 72.76) * mm, "radius": 1.2 * mm});
            skCircle(sketch, "E6.16.26.0", {"center": v(40.88, 79.11) * mm, "radius": 1.2 * mm});
            skCircle(sketch, "E6.16.27.0", {"center": v(40.88, 85.46) * mm, "radius": 1.2 * mm});
            skCircle(sketch, "E6.17.0.0", {"center": v(47.23, -85.99) * mm, "radius": 1.2 * mm});
            skCircle(sketch, "E6.17.1.0", {"center": v(47.23, -79.64) * mm, "radius": 1.2 * mm});
            skCircle(sketch, "E6.17.2.0", {"center": v(47.23, -73.29) * mm, "radius": 1.2 * mm});
            skCircle(sketch, "E6.17.3.0", {"center": v(47.23, -66.94) * mm, "radius": 1.2 * mm});
            skCircle(sketch, "E6.17.4.0", {"center": v(47.23, -60.59) * mm, "radius": 1.2 * mm});
            skCircle(sketch, "E6.17.5.0", {"center": v(47.23, -54.24) * mm, "radius": 1.2 * mm});
            skCircle(sketch, "E6.17.6.0", {"center": v(47.23, -47.89) * mm, "radius": 1.2 * mm});
            skCircle(sketch, "E6.17.7.0", {"center": v(47.23, -41.54) * mm, "radius": 1.2 * mm});
            skCircle(sketch, "E6.17.8.0", {"center": v(47.23, -35.19) * mm, "radius": 1.2 * mm});
            skCircle(sketch, "E6.17.9.0", {"center": v(47.23, -28.84) * mm, "radius": 1.2 * mm});
            skCircle(sketch, "E6.17.10.0", {"center": v(47.23, -22.49) * mm, "radius": 1.2 * mm});
            skCircle(sketch, "E6.17.11.0", {"center": v(47.23, -16.14) * mm, "radius": 1.2 * mm});
            skCircle(sketch, "E6.17.12.0", {"center": v(47.23, -9.79) * mm, "radius": 1.2 * mm});
            skCircle(sketch, "E6.17.13.0", {"center": v(47.23, -3.44) * mm, "radius": 1.2 * mm});
            skCircle(sketch, "E6.17.14.0", {"center": v(47.23, 2.91) * mm, "radius": 1.2 * mm});
            skCircle(sketch, "E6.17.15.0", {"center": v(47.23, 9.26) * mm, "radius": 1.2 * mm});
            skCircle(sketch, "E6.17.16.0", {"center": v(47.23, 15.61) * mm, "radius": 1.2 * mm});
            skCircle(sketch, "E6.17.17.0", {"center": v(47.23, 21.96) * mm, "radius": 1.2 * mm});
            skCircle(sketch, "E6.17.18.0", {"center": v(47.23, 28.31) * mm, "radius": 1.2 * mm});
            skCircle(sketch, "E6.17.19.0", {"center": v(47.23, 34.66) * mm, "radius": 1.2 * mm});
            skCircle(sketch, "E6.17.20.0", {"center": v(47.23, 41.01) * mm, "radius": 1.2 * mm});
            skCircle(sketch, "E6.17.21.0", {"center": v(47.23, 47.36) * mm, "radius": 1.2 * mm});
            skCircle(sketch, "E6.17.22.0", {"center": v(47.23, 53.71) * mm, "radius": 1.2 * mm});
            skCircle(sketch, "E6.17.23.0", {"center": v(47.23, 60.06) * mm, "radius": 1.2 * mm});
            skCircle(sketch, "E6.17.24.0", {"center": v(47.23, 66.41) * mm, "radius": 1.2 * mm});
            skCircle(sketch, "E6.17.25.0", {"center": v(47.23, 72.76) * mm, "radius": 1.2 * mm});
            skCircle(sketch, "E6.17.26.0", {"center": v(47.23, 79.11) * mm, "radius": 1.2 * mm});
            skCircle(sketch, "E6.17.27.0", {"center": v(47.23, 85.46) * mm, "radius": 1.2 * mm});
            skCircle(sketch, "E6.18.0.0", {"center": v(53.58, -85.99) * mm, "radius": 1.2 * mm});
            skCircle(sketch, "E6.18.1.0", {"center": v(53.58, -79.64) * mm, "radius": 1.2 * mm});
            skCircle(sketch, "E6.18.2.0", {"center": v(53.58, -73.29) * mm, "radius": 1.2 * mm});
            skCircle(sketch, "E6.18.3.0", {"center": v(53.58, -66.94) * mm, "radius": 1.2 * mm});
            skCircle(sketch, "E6.18.4.0", {"center": v(53.58, -60.59) * mm, "radius": 1.2 * mm});
            skCircle(sketch, "E6.18.5.0", {"center": v(53.58, -54.24) * mm, "radius": 1.2 * mm});
            skCircle(sketch, "E6.18.6.0", {"center": v(53.58, -47.89) * mm, "radius": 1.2 * mm});
            skCircle(sketch, "E6.18.7.0", {"center": v(53.58, -41.54) * mm, "radius": 1.2 * mm});
            skCircle(sketch, "E6.18.8.0", {"center": v(53.58, -35.19) * mm, "radius": 1.2 * mm});
            skCircle(sketch, "E6.18.9.0", {"center": v(53.58, -28.84) * mm, "radius": 1.2 * mm});
            skCircle(sketch, "E6.18.10.0", {"center": v(53.58, -22.49) * mm, "radius": 1.2 * mm});
            skCircle(sketch, "E6.18.11.0", {"center": v(53.58, -16.14) * mm, "radius": 1.2 * mm});
            skCircle(sketch, "E6.18.12.0", {"center": v(53.58, -9.79) * mm, "radius": 1.2 * mm});
            skCircle(sketch, "E6.18.13.0", {"center": v(53.58, -3.44) * mm, "radius": 1.2 * mm});
            skCircle(sketch, "E6.18.14.0", {"center": v(53.58, 2.91) * mm, "radius": 1.2 * mm});
            skCircle(sketch, "E6.18.15.0", {"center": v(53.58, 9.26) * mm, "radius": 1.2 * mm});
            skCircle(sketch, "E6.18.16.0", {"center": v(53.58, 15.61) * mm, "radius": 1.2 * mm});
            skCircle(sketch, "E6.18.17.0", {"center": v(53.58, 21.96) * mm, "radius": 1.2 * mm});
            skCircle(sketch, "E6.18.18.0", {"center": v(53.58, 28.31) * mm, "radius": 1.2 * mm});
            skCircle(sketch, "E6.18.19.0", {"center": v(53.58, 34.66) * mm, "radius": 1.2 * mm});
            skCircle(sketch, "E6.18.20.0", {"center": v(53.58, 41.01) * mm, "radius": 1.2 * mm});
            skCircle(sketch, "E6.18.21.0", {"center": v(53.58, 47.36) * mm, "radius": 1.2 * mm});
            skCircle(sketch, "E6.18.22.0", {"center": v(53.58, 53.71) * mm, "radius": 1.2 * mm});
            skCircle(sketch, "E6.18.23.0", {"center": v(53.58, 60.06) * mm, "radius": 1.2 * mm});
            skCircle(sketch, "E6.18.24.0", {"center": v(53.58, 66.41) * mm, "radius": 1.2 * mm});
            skCircle(sketch, "E6.18.25.0", {"center": v(53.58, 72.76) * mm, "radius": 1.2 * mm});
            skCircle(sketch, "E6.18.26.0", {"center": v(53.58, 79.11) * mm, "radius": 1.2 * mm});
            skCircle(sketch, "E6.18.27.0", {"center": v(53.58, 85.46) * mm, "radius": 1.2 * mm});
            skCircle(sketch, "E6.19.0.0", {"center": v(59.93, -85.99) * mm, "radius": 1.2 * mm});
            skCircle(sketch, "E6.19.1.0", {"center": v(59.93, -79.64) * mm, "radius": 1.2 * mm});
            skCircle(sketch, "E6.19.2.0", {"center": v(59.93, -73.29) * mm, "radius": 1.2 * mm});
            skCircle(sketch, "E6.19.3.0", {"center": v(59.93, -66.94) * mm, "radius": 1.2 * mm});
            skCircle(sketch, "E6.19.4.0", {"center": v(59.93, -60.59) * mm, "radius": 1.2 * mm});
            skCircle(sketch, "E6.19.5.0", {"center": v(59.93, -54.24) * mm, "radius": 1.2 * mm});
            skCircle(sketch, "E6.19.6.0", {"center": v(59.93, -47.89) * mm, "radius": 1.2 * mm});
            skCircle(sketch, "E6.19.7.0", {"center": v(59.93, -41.54) * mm, "radius": 1.2 * mm});
            skCircle(sketch, "E6.19.8.0", {"center": v(59.93, -35.19) * mm, "radius": 1.2 * mm});
            skCircle(sketch, "E6.19.9.0", {"center": v(59.93, -28.84) * mm, "radius": 1.2 * mm});
            skCircle(sketch, "E6.19.10.0", {"center": v(59.93, -22.49) * mm, "radius": 1.2 * mm});
            skCircle(sketch, "E6.19.11.0", {"center": v(59.93, -16.14) * mm, "radius": 1.2 * mm});
            skCircle(sketch, "E6.19.12.0", {"center": v(59.93, -9.79) * mm, "radius": 1.2 * mm});
            skCircle(sketch, "E6.19.13.0", {"center": v(59.93, -3.44) * mm, "radius": 1.2 * mm});
            skCircle(sketch, "E6.19.14.0", {"center": v(59.93, 2.91) * mm, "radius": 1.2 * mm});
            skCircle(sketch, "E6.19.15.0", {"center": v(59.93, 9.26) * mm, "radius": 1.2 * mm});
            skCircle(sketch, "E6.19.16.0", {"center": v(59.93, 15.61) * mm, "radius": 1.2 * mm});
            skCircle(sketch, "E6.19.17.0", {"center": v(59.93, 21.96) * mm, "radius": 1.2 * mm});
            skCircle(sketch, "E6.19.18.0", {"center": v(59.93, 28.31) * mm, "radius": 1.2 * mm});
            skCircle(sketch, "E6.19.19.0", {"center": v(59.93, 34.66) * mm, "radius": 1.2 * mm});
            skCircle(sketch, "E6.19.20.0", {"center": v(59.93, 41.01) * mm, "radius": 1.2 * mm});
            skCircle(sketch, "E6.19.21.0", {"center": v(59.93, 47.36) * mm, "radius": 1.2 * mm});
            skCircle(sketch, "E6.19.22.0", {"center": v(59.93, 53.71) * mm, "radius": 1.2 * mm});
            skCircle(sketch, "E6.19.23.0", {"center": v(59.93, 60.06) * mm, "radius": 1.2 * mm});
            skCircle(sketch, "E6.19.24.0", {"center": v(59.93, 66.41) * mm, "radius": 1.2 * mm});
            skCircle(sketch, "E6.19.25.0", {"center": v(59.93, 72.76) * mm, "radius": 1.2 * mm});
            skCircle(sketch, "E6.19.26.0", {"center": v(59.93, 79.11) * mm, "radius": 1.2 * mm});
            skCircle(sketch, "E6.19.27.0", {"center": v(59.93, 85.46) * mm, "radius": 1.2 * mm});
            skLineSegment(sketch, "E6.direction1", {"start": v(-60.72, -85.99) * mm, "end": v(-54.37, -85.99) * mm, "construction": true});
            skLineSegment(sketch, "E6.direction2", {"start": v(-60.72, -85.99) * mm, "end": v(-60.72, -79.64) * mm, "construction": true});
            skSolve(sketch);
        }
        {
            var Q0;
            Q0 = qSketchRegion(id + "F2", true);
            extrude(context, id + "F3", {"entities" : qUnion([Q0]), "operationType" : NewBodyOperationType.REMOVE, "endBound" : BoundingType.THROUGH_ALL, "oppositeDirection" : true, "depth" : 25.4 * mm});
        }
    });
